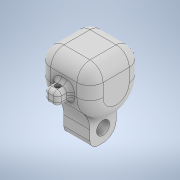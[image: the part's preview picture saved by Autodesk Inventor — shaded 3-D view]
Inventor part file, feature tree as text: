
AUTODESK INVENTOR PART (.ipt)
format: ipt  version: 2022 (Build 260153000, 153)  size: 351,232 bytes
history: native  units: mm
features: fillet x9, extrude x5, sketch x5
ambient origin geometry x8: Origin, YZ Plane, XZ Plane, XY Plane, X Axis, Y Axis, Z Axis, Center Point
bodies: Solide1 (feature_tree)
feature tree (19):
  extrude  "Extrusion1"  Depth=20.0mm
  extrude  "Extrusion2"  Depth=20.0mm
  extrude  "Extrusion3"  Depth=20.0mm TaperAngle=0.0deg
  fillet  "Congé1"  Radius=10.0mm
  fillet  "Congé2"  Radius=10.0mm
  fillet  "Congé5"  Radius=10.0mm
  fillet  "Congé6"  Radius=20.0mm
  fillet  "Congé7"  Radius=5.0mm
  fillet  "Congé9"  Radius=20.0mm
  fillet  "Congé10"  Radius=5.0mm
  extrude  "Extrusion6"  Depth=10.0mm
  extrude  "Extrusion7"  Depth=5.0mm
  fillet  "Congé11"  Radius=5.0mm
  fillet  "Congé12"  Radius=5.0mm
  sketch  "Esquisse1"
  sketch  "Esquisse3"
  sketch  "Esquisse4"
  sketch  "Esquisse10"
  sketch  "Esquisse11"
